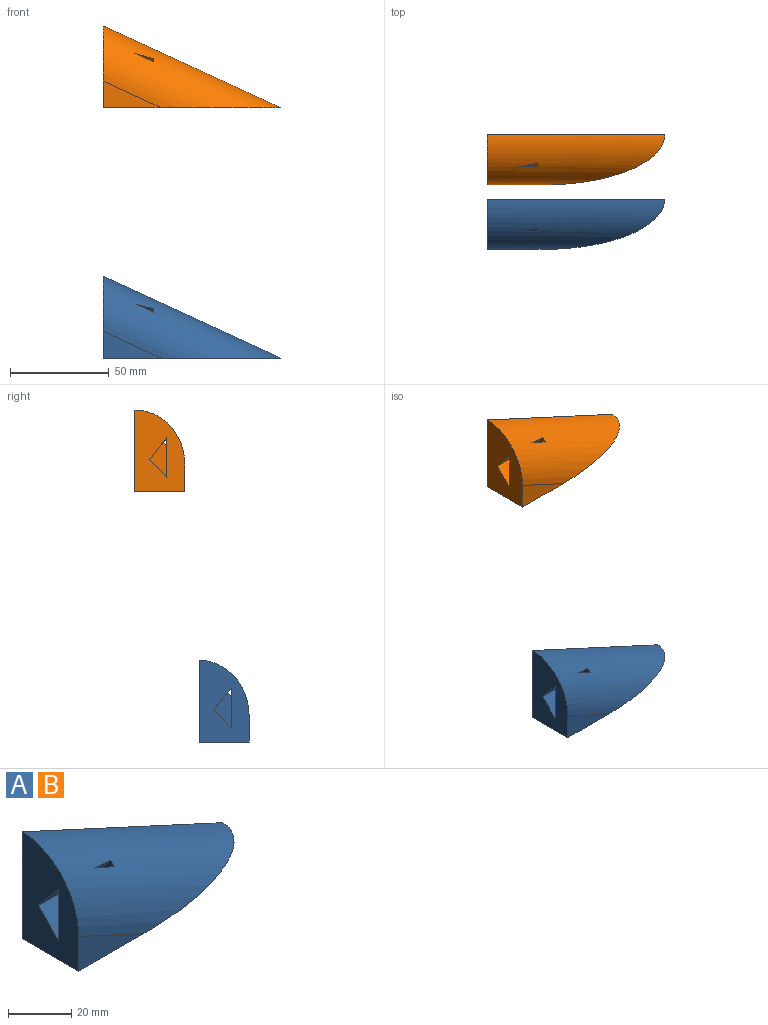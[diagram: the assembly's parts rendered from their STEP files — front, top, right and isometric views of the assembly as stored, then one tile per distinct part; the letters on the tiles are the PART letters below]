
ASSEMBLY  parts=2 mates=1
PART A: 9 faces, bbox 100.6x25.4x64.5 mm
  f0: plane 41.47x25.4mm, normal (-1,0,0), area 813.5mm2, adj f1,f2,f3,f4,f5,f6,f7
  f1: plane 89.99x25.4mm, normal (0,0,-1), area 1955mm2, adj f0,f2,f3,f4
  f2: plane 29.3x13.5mm, normal (0,-1,0), area 197.9mm2, adj f0,f1,f4
  f3: plane 89.99x41.47mm, normal (0,1,0), area 1866mm2, adj f0,f1,f4
  f4: cylinder r=25.4mm len=100.62mm, axis (0.91,0,-0.42), area 2973mm2, adj f0,f1,f2,f3,f5,f7,f8
  f5: plane 25.4x10.76mm, normal (0,-0.77,-0.63), area 340mm2, adj f0,f4,f6,f7,f8
  f6: plane 25.4x9.09mm, normal (0,-0.72,0.7), area 321.6mm2, adj f0,f5,f7,f8
  f7: plane 25.4x19.85mm, normal (0,1,0), area 486.9mm2, adj f0,f4,f5,f6,f8
  f8: plane 17.47x8.81mm, normal (-1,0,0), area 83.6mm2, adj f4,f5,f6,f7
PART B: same geometry as A
PLACE A t=(-14.45,-1.85,8.93)mm fixed
PLACE B t=(-14.45,30.7,135.93)mm
MATE planar A.f0 <-> B.f0  axis (-1,0,0) through (-104.44,-18.08,36.23)mm
